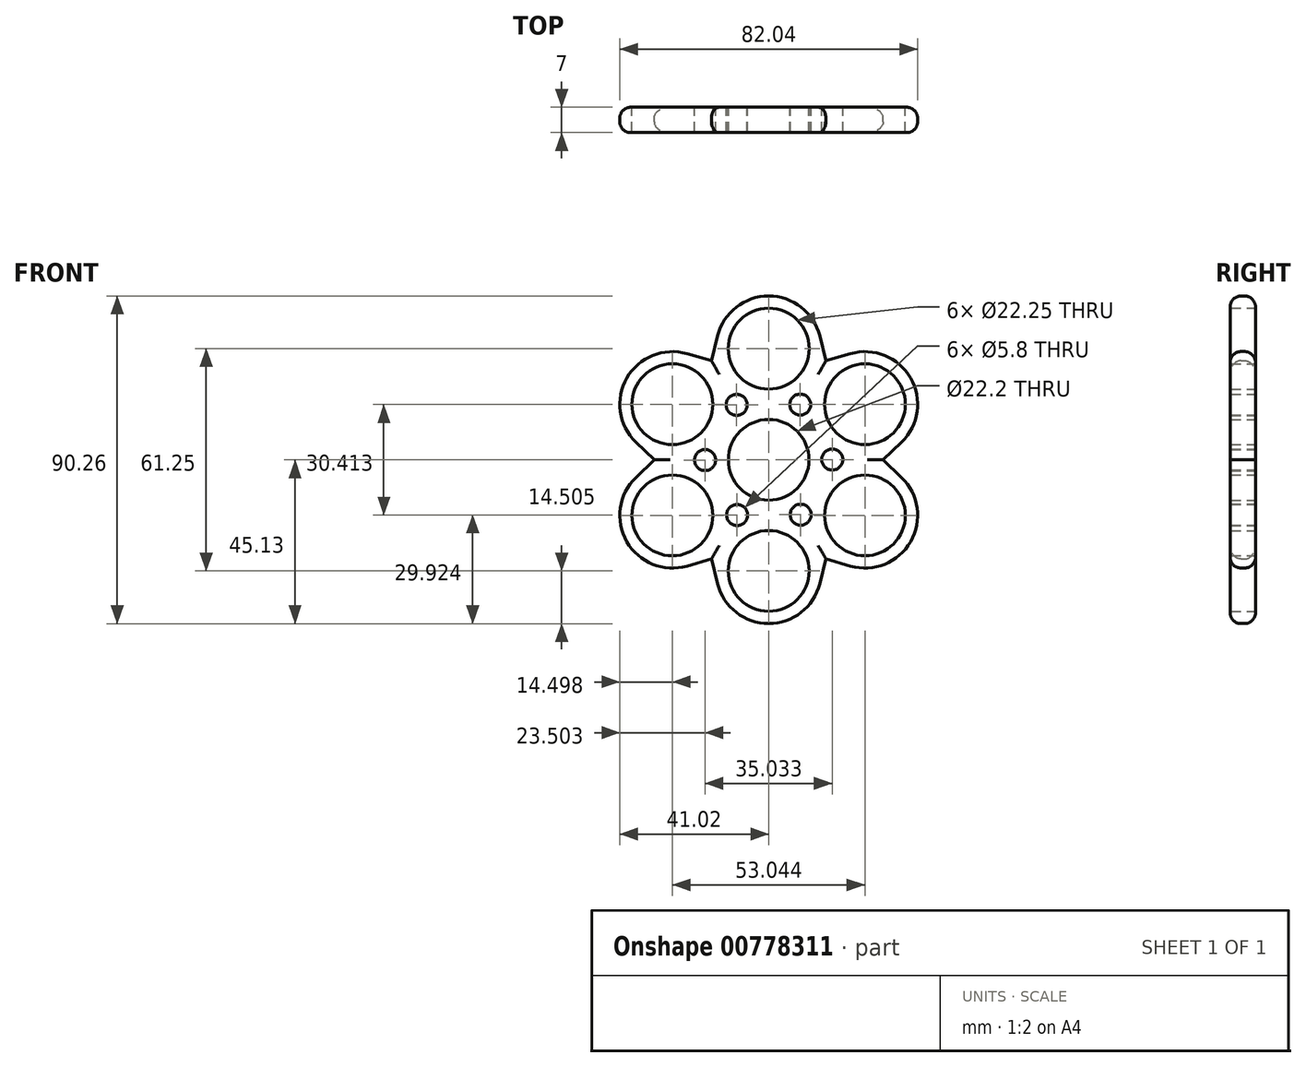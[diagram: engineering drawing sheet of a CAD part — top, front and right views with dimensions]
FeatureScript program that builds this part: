
annotation { "Feature Type Name" : "Feature", "Feature Type Description" : "" }
export const myFeature = defineFeature(function(context is Context, id is Id, definition is map)
    precondition{}
    {
        {
            var Q0;
            Q0=qCreatedBy(makeId("Front.planeOp"),FACE);
            var sketch = newSketch(context, id + "F0", { "sketchPlane" : qUnion([Q0])});
            skCircle(sketch, "E0", {"center": v(0, 0) * mm, "radius": 11.1 * mm});
            skCircle(sketch, "E1", {"center": v(0, 30.63) * mm, "radius": 11.12 * mm});
            skCircle(sketch, "E2", {"center": v(0, 30.63) * mm, "radius": 14.5 * mm});
            skCircle(sketch, "E3.1.0", {"center": v(-26.52, 15.31) * mm, "radius": 14.5 * mm});
            skCircle(sketch, "E3.1.1", {"center": v(0, 0) * mm, "radius": 14 * mm});
            skCircle(sketch, "E3.1.2", {"center": v(-26.52, 15.31) * mm, "radius": 11.12 * mm});
            skCircle(sketch, "E3.2.0", {"center": v(-26.52, -15.31) * mm, "radius": 14.5 * mm});
            skCircle(sketch, "E3.2.1", {"center": v(0, 0) * mm, "radius": 14 * mm});
            skCircle(sketch, "E3.2.2", {"center": v(-26.52, -15.31) * mm, "radius": 11.12 * mm});
            skArc(sketch, "E3.3.0", {"start": v(-9.2, -19.42) * mm, "mid": v(8.04, -42.7) * mm, "end": v(-6.78, -17.81) * mm});
            skCircle(sketch, "E3.3.2", {"center": v(0, -30.63) * mm, "radius": 11.12 * mm});
            skCircle(sketch, "E3.4.0", {"center": v(26.52, -15.31) * mm, "radius": 14.5 * mm});
            skCircle(sketch, "E3.4.2", {"center": v(26.52, -15.31) * mm, "radius": 11.12 * mm});
            skArc(sketch, "E3.5.0", {"start": v(36.6, 4.89) * mm, "mid": v(33.1, 28.23) * mm, "end": v(12.17, 17.35) * mm});
            skArc(sketch, "E3.5.1", {"start": v(-14, -0.1) * mm, "mid": v(-6.96, -12.15) * mm, "end": v(7, -12.12) * mm});
            skCircle(sketch, "E3.5.2", {"center": v(26.52, 15.31) * mm, "radius": 11.12 * mm});
            skArc(sketch, "E4", {"start": v(12.05, 14.34) * mm, "mid": v(12.51, 15.83) * mm, "end": v(12.17, 17.35) * mm});
            skPoint(sketch, "E5.center", {"position": v(0.03, -0.25) * mm});
            skArc(sketch, "E6.1.5.0", {"start": v(20.38, 2.18) * mm, "mid": v(20.12, 2.32) * mm, "end": v(19.84, 2.44) * mm});
            skLineSegment(sketch, "E7", {"start": v(0, 0) * mm, "end": v(-8.82, 10.87) * mm, "construction": true});
            skLineSegment(sketch, "E8", {"start": v(0, 0) * mm, "end": v(-18.73, -0.13) * mm, "construction": true});
            skLineSegment(sketch, "E9", {"start": v(-18.73, -0.13) * mm, "end": v(-54.47, -0.13) * mm, "construction": true});
            skLineSegment(sketch, "E10", {"start": v(-36.6, 4.89) * mm, "end": v(-31.54, 0) * mm});
            skPoint(sketch, "E10.startSnap0", {"position": v(-36.6, -0.13) * mm});
            skLineSegment(sketch, "E11", {"start": v(-31.54, 0) * mm, "end": v(-36.6, -4.89) * mm});
            skPoint(sketch, "E12.1.0", {"position": v(-18.19, -31.76) * mm});
            skLineSegment(sketch, "E12.1.1", {"start": v(-15.77, -27.32) * mm, "end": v(-14.07, -34.14) * mm});
            skLineSegment(sketch, "E12.1.2", {"start": v(-22.53, -29.25) * mm, "end": v(-15.77, -27.32) * mm});
            skPoint(sketch, "E12.2.0", {"position": v(18.41, -31.63) * mm});
            skLineSegment(sketch, "E12.2.1", {"start": v(15.77, -27.32) * mm, "end": v(22.53, -29.25) * mm});
            skLineSegment(sketch, "E12.2.2", {"start": v(14.07, -34.14) * mm, "end": v(15.77, -27.32) * mm});
            skPoint(sketch, "E12.3.0", {"position": v(36.6, 0.13) * mm});
            skLineSegment(sketch, "E12.3.1", {"start": v(31.54, 0) * mm, "end": v(36.6, 4.89) * mm});
            skLineSegment(sketch, "E12.3.2", {"start": v(36.6, -4.89) * mm, "end": v(31.54, 0) * mm});
            skPoint(sketch, "E12.4.0", {"position": v(18.19, 31.76) * mm});
            skLineSegment(sketch, "E12.4.1", {"start": v(15.77, 27.32) * mm, "end": v(14.07, 34.14) * mm});
            skLineSegment(sketch, "E12.4.2", {"start": v(22.53, 29.25) * mm, "end": v(15.77, 27.32) * mm});
            skPoint(sketch, "E12.5.0", {"position": v(-18.41, 31.63) * mm});
            skLineSegment(sketch, "E12.5.1", {"start": v(-15.77, 27.32) * mm, "end": v(-22.53, 29.25) * mm});
            skLineSegment(sketch, "E12.5.2", {"start": v(-14.07, 34.14) * mm, "end": v(-15.77, 27.32) * mm});
            skCircle(sketch, "E13", {"center": v(-8.82, 15.13) * mm, "radius": 2.9 * mm});
            skCircle(sketch, "E14.1.0", {"center": v(-17.52, -0.07) * mm, "radius": 2.9 * mm});
            skCircle(sketch, "E14.2.0", {"center": v(-8.7, -15.2) * mm, "radius": 2.9 * mm});
            skCircle(sketch, "E14.3.0", {"center": v(8.82, -15.13) * mm, "radius": 2.9 * mm});
            skCircle(sketch, "E14.4.0", {"center": v(17.52, 0.07) * mm, "radius": 2.9 * mm});
            skCircle(sketch, "E14.5.0", {"center": v(8.7, 15.2) * mm, "radius": 2.9 * mm});
            skArc(sketch, "E15.trimOffspring", {"start": v(12.05, 14.34) * mm, "mid": v(14.39, 7.37) * mm, "end": v(19.84, 2.44) * mm});
            skSolve(sketch);
        }
        {
            var Q0;
            Q0 = qSketchRegion(id + "F0", true);
            var Q1;
            Q1=makeQuery(id+"F0.imprint","IMPRINT",FACE,{"disambiguationData":[TD([[makeQuery(id+"F0.imprint","IMPRINT",EDGE,{"derivedFrom":sQuery(id+"F0.wireOp",EDGE,"E0")}),-1.0]])]});
            extrude(context, id + "F1", {"entities" : qUnion([Q0, Q1]), "depth" : 7 * mm, "offsetDistance" : 25 * mm});
        }
        {
            var Q0;
            Q0=makeQuery(id+"F1.opExtrude","CAP_EDGE",EDGE,{"disambiguationData":[OSD([sQuery(id+"F0.wireOp",EDGE,"E3.2.0")])],"isStart":false});
            var Q1;
            Q1=makeQuery(id+"F1.opExtrude","CAP_EDGE",EDGE,{"disambiguationData":[OSD([sQuery(id+"F0.wireOp",EDGE,"E3.1.0")])],"isStart":false});
            var Q2;
            Q2=makeQuery(id+"F1.opExtrude","CAP_EDGE",EDGE,{"disambiguationData":[OSD([sQuery(id+"F0.wireOp",EDGE,"E3.3.0")])],"isStart":false});
            var Q3;
            Q3=makeQuery(id+"F1.opExtrude","CAP_EDGE",EDGE,{"disambiguationData":[OSD([sQuery(id+"F0.wireOp",EDGE,"E3.4.0")])],"isStart":false});
            var Q4;
            Q4=makeQuery(id+"F1.opExtrude","CAP_EDGE",EDGE,{"disambiguationData":[OSD([sQuery(id+"F0.wireOp",EDGE,"E3.5.0")])],"isStart":false});
            var Q5;
            Q5=makeQuery(id+"F1.opExtrude","CAP_EDGE",EDGE,{"disambiguationData":[OSD([sQuery(id+"F0.wireOp",EDGE,"E2")])],"isStart":false});
            var Q6;
            Q6=makeQuery(id+"F1.opExtrude","CAP_EDGE",EDGE,{"disambiguationData":[OSD([sQuery(id+"F0.wireOp",EDGE,"E3.3.0")])],"isStart":true});
            var Q7;
            Q7=makeQuery(id+"F1.opExtrude","CAP_EDGE",EDGE,{"disambiguationData":[OSD([sQuery(id+"F0.wireOp",EDGE,"E3.4.0")])],"isStart":true});
            var Q8;
            Q8=makeQuery(id+"F1.opExtrude","CAP_EDGE",EDGE,{"disambiguationData":[OSD([sQuery(id+"F0.wireOp",EDGE,"E3.1.0")])],"isStart":true});
            var Q9;
            Q9=makeQuery(id+"F1.opExtrude","CAP_EDGE",EDGE,{"disambiguationData":[OSD([sQuery(id+"F0.wireOp",EDGE,"E2")])],"isStart":true});
            var Q10;
            Q10=makeQuery(id+"F1.opExtrude","CAP_EDGE",EDGE,{"disambiguationData":[OSD([sQuery(id+"F0.wireOp",EDGE,"E3.2.0")])],"isStart":true});
            var Q11;
            Q11=makeQuery(id+"F1.opExtrude","CAP_EDGE",EDGE,{"disambiguationData":[OSD([sQuery(id+"F0.wireOp",EDGE,"E3.5.0")])],"isStart":true});
            fillet(context, id + "F2", {"entities" : qUnion([Q0, Q1, Q2, Q3, Q4, Q5, Q6, Q7, Q8, Q9, Q10, Q11]), "radius" : 3 * mm, "tangentPropagation" : true, "allowEdgeOverflow" : false});
        }
    });
